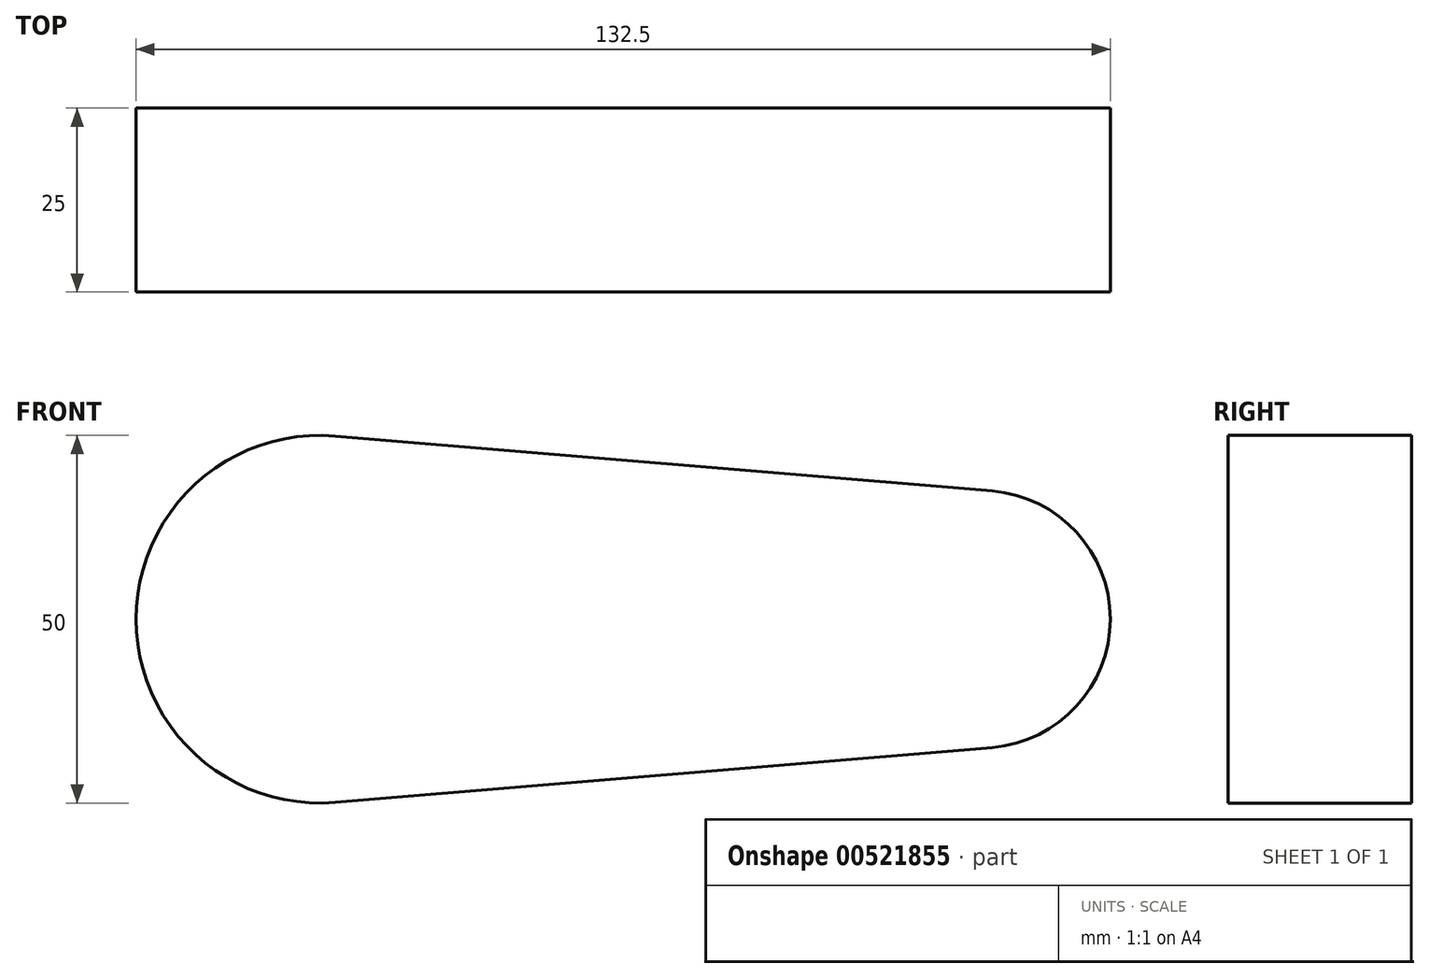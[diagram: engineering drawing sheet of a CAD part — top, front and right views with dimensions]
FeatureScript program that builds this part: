
annotation { "Feature Type Name" : "Feature", "Feature Type Description" : "" }
export const myFeature = defineFeature(function(context is Context, id is Id, definition is map)
    precondition{}
    {
        {
            var Q0;
            Q0=qCreatedBy(makeId("Front.planeOp"),FACE);
            var sketch = newSketch(context, id + "F0", { "sketchPlane" : qUnion([Q0])});
            skCircle(sketch, "E0", {"center": v(0, 0) * mm, "radius": 25 * mm});
            skCircle(sketch, "E1", {"center": v(90, 0) * mm, "radius": 17.5 * mm});
            skLineSegment(sketch, "E2", {"start": v(2.08, -24.91) * mm, "end": v(91.46, -17.44) * mm});
            skLineSegment(sketch, "E3", {"start": v(2.08, 24.91) * mm, "end": v(91.46, 17.44) * mm});
            skSolve(sketch);
        }
        {
            var Q0;
            {var subQ0=sQuery(id+"F0.wireOp",EDGE,"E1");var subQ1=makeQuery(id+"F0.imprint","INTERSECT",VERTEX,{"derivedFrom":[subQ0,sQuery(id+"F0.wireOp",EDGE,"E2")]});Q0=makeQuery(id+"F0.imprint","IMPRINT",FACE,{"disambiguationData":[TD([[makeQuery(id+"F0.imprint","IMPRINT",EDGE,{"disambiguationData":[TD([[subQ1,1.0]])],"derivedFrom":subQ0}),1.0]])]});}
            var Q1;
            {var subQ0=sQuery(id+"F0.wireOp",EDGE,"E0");var subQ1=makeQuery(id+"F0.imprint","INTERSECT",VERTEX,{"derivedFrom":[subQ0,sQuery(id+"F0.wireOp",EDGE,"E2")]});Q1=makeQuery(id+"F0.imprint","IMPRINT",FACE,{"disambiguationData":[TD([[makeQuery(id+"F0.imprint","IMPRINT",EDGE,{"disambiguationData":[TD([[subQ1,1.0]])],"derivedFrom":subQ0}),1.0]])]});}
            var Q2;
            {var subQ0=sQuery(id+"F0.wireOp",EDGE,"E2");Q2=makeQuery(id+"F0.imprint","IMPRINT",FACE,{"disambiguationData":[TD([[makeQuery(id+"F0.imprint","IMPRINT",EDGE,{"derivedFrom":subQ0}),1.0]])]});}
            extrude(context, id + "F1", {"entities" : qUnion([Q0, Q1, Q2]), "depth" : 25 * mm, "offsetDistance" : 25 * mm});
        }
    });
